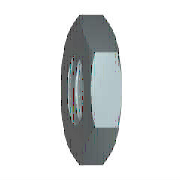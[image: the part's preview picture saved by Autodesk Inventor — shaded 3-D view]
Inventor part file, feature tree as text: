
AUTODESK INVENTOR PART (.ipt)
format: ipt  version: 2022 (Build 260153000, 153)  size: 164,352 bytes
history: native  units: mm (DEFAULTED — no unit token found)
features: sketch x3, extrude x1, chamfer x1, hole x1, other x1, plane x1
ambient origin geometry x7: Origin, YZ Plane, XZ Plane, X Axis, Y Axis, Z Axis, Center Point
bodies: Solid1 (feature_tree)
feature tree (8):
  extrude  "Cuerpo"  Depth=1.8mm
  chamfer  "Chaflán1"  Angle=30.0deg  [1 undecoded]
  hole  "Rosca"  [1 undecoded]
  other  "Work Axis1"
  plane  "Work Plane1"
  sketch  "Boceto1"  dims[d0=6.350853mm d1=1.8mm]
  sketch  "Boceto2"  dims[d2=0.0mm]
  sketch  "Boceto3"  dims[d3=30.0deg d4=30.0deg d5=4.6mm d6=4.6mm d7=90.0deg d25=2.459mm d26=6.0mm d27=4.0mm d28=2.0mm d29=14.3117mm d30=8.0mm d31=20.594885mm d8=0.270633mm d9=30.0deg d10=0.270633mm d11=30.0deg d13=0.0mm d14=0.0mm d39=0.0mm d40=0.270633mm d41=0.270633mm d42=0.0mm]
note: 2 required parameter values undecoded (feature->parameter linkage not recoverable at this tier; creation-order binding heuristic only, values carry confidence <= 0.55)
